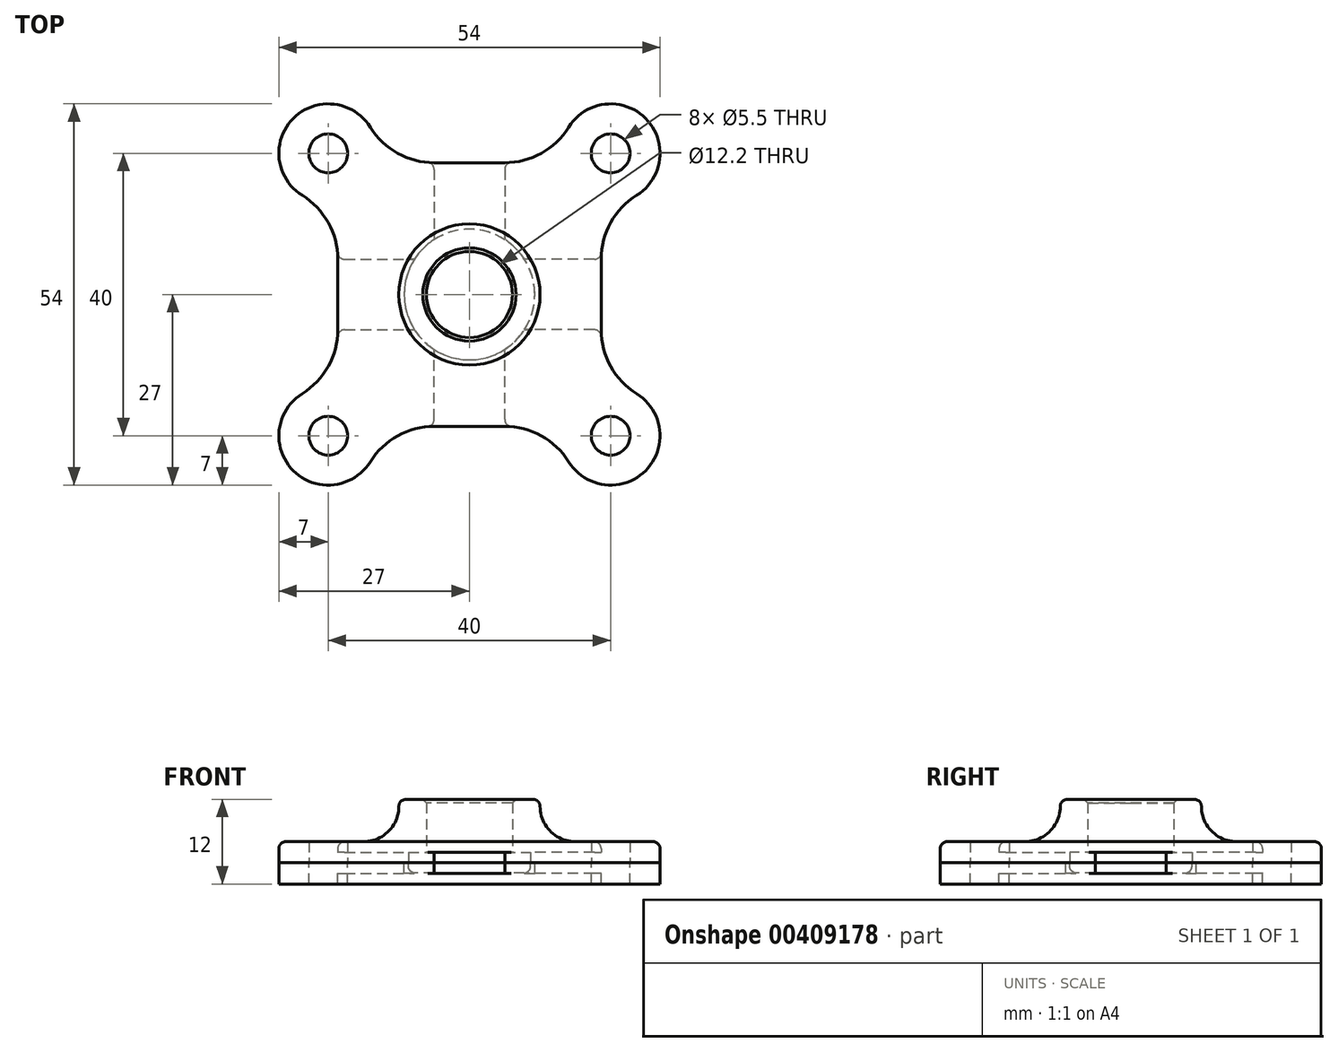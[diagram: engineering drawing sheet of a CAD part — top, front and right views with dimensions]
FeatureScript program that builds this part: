
annotation { "Feature Type Name" : "Feature", "Feature Type Description" : "" }
export const myFeature = defineFeature(function(context is Context, id is Id, definition is map)
    precondition{}
    {
        {
            var Q0;
            Q0=qCreatedBy(makeId("Top.planeOp"),FACE);
            var sketch = newSketch(context, id + "F0", { "sketchPlane" : qUnion([Q0])});
            skCircle(sketch, "E0", {"center": v(0, 0) * mm, "radius": 10 * mm});
            skCircle(sketch, "E1", {"center": v(0, 0) * mm, "radius": 6.1 * mm});
            skCircle(sketch, "E2", {"center": v(0, 0) * mm, "radius": 5 * mm});
            skCircle(sketch, "E3", {"center": v(0, 0) * mm, "radius": 9.25 * mm});
            skCircle(sketch, "E4", {"center": v(-20, 20) * mm, "radius": 2.75 * mm});
            skArc(sketch, "E5", {"start": v(-24.95, 24.95) * mm, "mid": v(-26.95, 19.2) * mm, "end": v(-23.7, 14.05) * mm});
            skLineSegment(sketch, "E6", {"start": v(-18.66, 5) * mm, "end": v(-8.66, 5) * mm});
            skArc(sketch, "E7", {"start": v(-23.7, 14.05) * mm, "mid": v(-20, 10.18) * mm, "end": v(-18.66, 5) * mm});
            skLineSegment(sketch, "E8", {"start": v(-20, 20) * mm, "end": v(0, 0) * mm, "construction": true});
            skLineSegment(sketch, "E9", {"start": v(-18.66, 5) * mm, "end": v(-18.66, 0) * mm});
            skArc(sketch, "E10.MirrorCS", {"start": v(-24.95, 24.95) * mm, "mid": v(-19.2, 26.95) * mm, "end": v(-14.05, 23.7) * mm});
            skArc(sketch, "E11.MirrorCS", {"start": v(-14.05, 23.7) * mm, "mid": v(-10.18, 20) * mm, "end": v(-5, 18.66) * mm});
            skLineSegment(sketch, "E12.MirrorCS", {"start": v(-5, 18.66) * mm, "end": v(-5, 8.66) * mm});
            skLineSegment(sketch, "E13.MirrorCS", {"start": v(-5, 18.66) * mm, "end": v(0, 18.66) * mm});
            skArc(sketch, "E14.1.0", {"start": v(-23.7, -14.05) * mm, "mid": v(-20, -10.18) * mm, "end": v(-18.66, -5) * mm});
            skLineSegment(sketch, "E14.1.1", {"start": v(-5, -18.66) * mm, "end": v(-5, -8.66) * mm});
            skArc(sketch, "E14.1.2", {"start": v(-24.95, -24.95) * mm, "mid": v(-26.95, -19.2) * mm, "end": v(-23.7, -14.05) * mm});
            skArc(sketch, "E14.1.3", {"start": v(-24.95, -24.95) * mm, "mid": v(-19.2, -26.95) * mm, "end": v(-14.05, -23.7) * mm});
            skLineSegment(sketch, "E14.1.4", {"start": v(-5, -18.66) * mm, "end": v(0, -18.66) * mm});
            skCircle(sketch, "E14.1.5", {"center": v(-20, -20) * mm, "radius": 2.75 * mm});
            skLineSegment(sketch, "E14.1.7", {"start": v(-18.66, -5) * mm, "end": v(-18.66, 0) * mm});
            skLineSegment(sketch, "E14.1.8", {"start": v(-18.66, -5) * mm, "end": v(-8.66, -5) * mm});
            skArc(sketch, "E14.1.9", {"start": v(-14.05, -23.7) * mm, "mid": v(-10.18, -20) * mm, "end": v(-5, -18.66) * mm});
            skLineSegment(sketch, "E14.1.10", {"start": v(-20, -20) * mm, "end": v(0, 0) * mm, "construction": true});
            skArc(sketch, "E14.2.0", {"start": v(14.05, -23.7) * mm, "mid": v(10.18, -20) * mm, "end": v(5, -18.66) * mm});
            skLineSegment(sketch, "E14.2.1", {"start": v(18.66, -5) * mm, "end": v(8.66, -5) * mm});
            skArc(sketch, "E14.2.2", {"start": v(24.95, -24.95) * mm, "mid": v(19.2, -26.95) * mm, "end": v(14.05, -23.7) * mm});
            skArc(sketch, "E14.2.3", {"start": v(24.95, -24.95) * mm, "mid": v(26.95, -19.2) * mm, "end": v(23.7, -14.05) * mm});
            skLineSegment(sketch, "E14.2.4", {"start": v(18.66, -5) * mm, "end": v(18.66, 0) * mm});
            skCircle(sketch, "E14.2.5", {"center": v(20, -20) * mm, "radius": 2.75 * mm});
            skLineSegment(sketch, "E14.2.7", {"start": v(5, -18.66) * mm, "end": v(0, -18.66) * mm});
            skLineSegment(sketch, "E14.2.8", {"start": v(5, -18.66) * mm, "end": v(5, -8.66) * mm});
            skArc(sketch, "E14.2.9", {"start": v(23.7, -14.05) * mm, "mid": v(20, -10.18) * mm, "end": v(18.66, -5) * mm});
            skLineSegment(sketch, "E14.2.10", {"start": v(20, -20) * mm, "end": v(0, 0) * mm, "construction": true});
            skArc(sketch, "E14.3.0", {"start": v(23.7, 14.05) * mm, "mid": v(20, 10.18) * mm, "end": v(18.66, 5) * mm});
            skLineSegment(sketch, "E14.3.1", {"start": v(5, 18.66) * mm, "end": v(5, 8.66) * mm});
            skArc(sketch, "E14.3.2", {"start": v(24.95, 24.95) * mm, "mid": v(26.95, 19.2) * mm, "end": v(23.7, 14.05) * mm});
            skArc(sketch, "E14.3.3", {"start": v(24.95, 24.95) * mm, "mid": v(19.2, 26.95) * mm, "end": v(14.05, 23.7) * mm});
            skLineSegment(sketch, "E14.3.4", {"start": v(5, 18.66) * mm, "end": v(0, 18.66) * mm});
            skCircle(sketch, "E14.3.5", {"center": v(20, 20) * mm, "radius": 2.75 * mm});
            skLineSegment(sketch, "E14.3.7", {"start": v(18.66, 5) * mm, "end": v(18.66, 0) * mm});
            skLineSegment(sketch, "E14.3.8", {"start": v(18.66, 5) * mm, "end": v(8.66, 5) * mm});
            skArc(sketch, "E14.3.9", {"start": v(14.05, 23.7) * mm, "mid": v(10.18, 20) * mm, "end": v(5, 18.66) * mm});
            skLineSegment(sketch, "E14.3.10", {"start": v(20, 20) * mm, "end": v(0, 0) * mm, "construction": true});
            skSolve(sketch);
        }
        {
            var Q0;
            {var subQ0=sQuery(id+"F0.wireOp",EDGE,"E14.2.1");Q0=makeQuery(id+"F0.imprint","IMPRINT",FACE,{"disambiguationData":[TD([[makeQuery(id+"F0.imprint","IMPRINT",EDGE,{"derivedFrom":subQ0}),-1.0]])]});}
            var Q1;
            Q1=makeQuery(id+"F0.imprint","IMPRINT",FACE,{"disambiguationData":[TD([[makeQuery(id+"F0.imprint","IMPRINT",EDGE,{"derivedFrom":sQuery(id+"F0.wireOp",EDGE,"E14.3.0")}),-1.0]])]});
            var Q2;
            Q2=makeQuery(id+"F0.imprint","IMPRINT",FACE,{"disambiguationData":[TD([[makeQuery(id+"F0.imprint","IMPRINT",EDGE,{"derivedFrom":sQuery(id+"F0.wireOp",EDGE,"E14.2.0")}),-1.0]])]});
            var Q3;
            Q3=makeQuery(id+"F0.imprint","IMPRINT",FACE,{"disambiguationData":[TD([[makeQuery(id+"F0.imprint","IMPRINT",EDGE,{"derivedFrom":sQuery(id+"F0.wireOp",EDGE,"E4")}),-1.0]])]});
            var Q4;
            Q4=makeQuery(id+"F0.imprint","IMPRINT",FACE,{"disambiguationData":[TD([[makeQuery(id+"F0.imprint","IMPRINT",EDGE,{"derivedFrom":sQuery(id+"F0.wireOp",EDGE,"E3")}),-1.0]])]});
            var Q5;
            Q5=makeQuery(id+"F0.imprint","IMPRINT",FACE,{"disambiguationData":[TD([[makeQuery(id+"F0.imprint","IMPRINT",EDGE,{"derivedFrom":sQuery(id+"F0.wireOp",EDGE,"E14.1.0")}),-1.0]])]});
            var Q6;
            {var subQ0=sQuery(id+"F0.wireOp",EDGE,"E14.1.1");Q6=makeQuery(id+"F0.imprint","IMPRINT",FACE,{"disambiguationData":[TD([[makeQuery(id+"F0.imprint","IMPRINT",EDGE,{"derivedFrom":subQ0}),-1.0]])]});}
            var Q7;
            Q7=makeQuery(id+"F0.imprint","IMPRINT",FACE,{"disambiguationData":[TD([[makeQuery(id+"F0.imprint","IMPRINT",EDGE,{"derivedFrom":sQuery(id+"F0.wireOp",EDGE,"E1")}),-1.0]])]});
            var Q8;
            {var subQ0=sQuery(id+"F0.wireOp",EDGE,"E6");Q8=makeQuery(id+"F0.imprint","IMPRINT",FACE,{"disambiguationData":[TD([[makeQuery(id+"F0.imprint","IMPRINT",EDGE,{"derivedFrom":subQ0}),-1.0]])]});}
            var Q9;
            {var subQ1=sQuery(id+"F0.wireOp",EDGE,"E12.MirrorCS");Q9=makeQuery(id+"F0.imprint","IMPRINT",FACE,{"disambiguationData":[TD([[makeQuery(id+"F0.imprint","IMPRINT",EDGE,{"derivedFrom":subQ1}),1.0]])]});}
            extrude(context, id + "F1", {"entities" : qUnion([Q0, Q1, Q2, Q3, Q4, Q5, Q6, Q7, Q8, Q9]), "depth" : 3 * mm, "offsetDistance" : 25 * mm});
        }
        {
            var Q0;
            Q0=makeQuery(id+"F0.imprint","IMPRINT",FACE,{"disambiguationData":[TD([[makeQuery(id+"F0.imprint","IMPRINT",EDGE,{"derivedFrom":sQuery(id+"F0.wireOp",EDGE,"E0")}),1.0]])]});
            var Q1;
            Q1=makeQuery(id+"F0.imprint","IMPRINT",FACE,{"disambiguationData":[TD([[makeQuery(id+"F0.imprint","IMPRINT",EDGE,{"derivedFrom":sQuery(id+"F0.wireOp",EDGE,"E1")}),-1.0]])]});
            extrude(context, id + "F2", {"entities" : qUnion([Q0, Q1]), "operationType" : NewBodyOperationType.ADD, "depth" : 9 * mm});
        }
        {
            var Q0;
            Q0=makeQuery(id+"F0.imprint","IMPRINT",FACE,{"disambiguationData":[TD([[makeQuery(id+"F0.imprint","IMPRINT",EDGE,{"derivedFrom":sQuery(id+"F0.wireOp",EDGE,"E1")}),-1.0]])]});
            var Q1;
            {var subQ0=sQuery(id+"F0.wireOp",EDGE,"5FznAjd5-Rlev-DzMA-E21E-VBbVsZXluKNu");Q1=makeQuery(id+"F0.imprint","IMPRINT",FACE,{"disambiguationData":[TD([[makeQuery(id+"F0.imprint","IMPRINT",EDGE,{"derivedFrom":subQ0}),1.0]])]});}
            var Q2;
            Q2=makeQuery(id+"F0.imprint","IMPRINT",FACE,{"disambiguationData":[TD([[makeQuery(id+"F0.imprint","IMPRINT",EDGE,{"derivedFrom":sQuery(id+"F0.wireOp",EDGE,"E3")}),-1.0]])]});
            var Q3;
            {var subQ1=sQuery(id+"F0.wireOp",EDGE,"bf5245d6-79ee-4a8b-a03c-ecbf48f2092a0.MirrorCS");Q3=makeQuery(id+"F0.imprint","IMPRINT",FACE,{"disambiguationData":[TD([[makeQuery(id+"F0.imprint","IMPRINT",EDGE,{"derivedFrom":subQ1}),-1.0]])]});}
            var Q4;
            {var subQ0=sQuery(id+"F0.wireOp",EDGE,"E14.1.1");Q4=makeQuery(id+"F0.imprint","IMPRINT",FACE,{"disambiguationData":[TD([[makeQuery(id+"F0.imprint","IMPRINT",EDGE,{"derivedFrom":subQ0}),-1.0]])]});}
            var Q5;
            {var subQ0=sQuery(id+"F0.wireOp",EDGE,"E6");Q5=makeQuery(id+"F0.imprint","IMPRINT",FACE,{"disambiguationData":[TD([[makeQuery(id+"F0.imprint","IMPRINT",EDGE,{"derivedFrom":subQ0}),-1.0]])]});}
            var Q6;
            {var subQ0=sQuery(id+"F0.wireOp",EDGE,"E14.2.1");Q6=makeQuery(id+"F0.imprint","IMPRINT",FACE,{"disambiguationData":[TD([[makeQuery(id+"F0.imprint","IMPRINT",EDGE,{"derivedFrom":subQ0}),-1.0]])]});}
            var Q7;
            {var subQ1=sQuery(id+"F0.wireOp",EDGE,"E12.MirrorCS");Q7=makeQuery(id+"F0.imprint","IMPRINT",FACE,{"disambiguationData":[TD([[makeQuery(id+"F0.imprint","IMPRINT",EDGE,{"derivedFrom":subQ1}),1.0]])]});}
            extrude(context, id + "F3", {"entities" : qUnion([Q0, Q1, Q2, Q3, Q4, Q5, Q6, Q7]), "operationType" : NewBodyOperationType.REMOVE, "depth" : 1.5 * mm, "offsetDistance" : 25 * mm});
        }
        {
            var Q0;
            Q0=makeQuery(id+"F0.imprint","IMPRINT",FACE,{"disambiguationData":[TD([[makeQuery(id+"F0.imprint","IMPRINT",EDGE,{"derivedFrom":sQuery(id+"F0.wireOp",EDGE,"E14.1.0")}),-1.0]])]});
            var Q1;
            {var subQ0=sQuery(id+"F0.wireOp",EDGE,"E14.1.1");Q1=makeQuery(id+"F0.imprint","IMPRINT",FACE,{"disambiguationData":[TD([[makeQuery(id+"F0.imprint","IMPRINT",EDGE,{"derivedFrom":subQ0}),-1.0]])]});}
            var Q2;
            Q2=makeQuery(id+"F0.imprint","IMPRINT",FACE,{"disambiguationData":[TD([[makeQuery(id+"F0.imprint","IMPRINT",EDGE,{"derivedFrom":sQuery(id+"F0.wireOp",EDGE,"E14.2.0")}),-1.0]])]});
            var Q3;
            {var subQ0=sQuery(id+"F0.wireOp",EDGE,"E14.2.1");Q3=makeQuery(id+"F0.imprint","IMPRINT",FACE,{"disambiguationData":[TD([[makeQuery(id+"F0.imprint","IMPRINT",EDGE,{"derivedFrom":subQ0}),-1.0]])]});}
            var Q4;
            Q4=makeQuery(id+"F0.imprint","IMPRINT",FACE,{"disambiguationData":[TD([[makeQuery(id+"F0.imprint","IMPRINT",EDGE,{"derivedFrom":sQuery(id+"F0.wireOp",EDGE,"E14.3.0")}),-1.0]])]});
            var Q5;
            {var subQ1=sQuery(id+"F0.wireOp",EDGE,"E12.MirrorCS");Q5=makeQuery(id+"F0.imprint","IMPRINT",FACE,{"disambiguationData":[TD([[makeQuery(id+"F0.imprint","IMPRINT",EDGE,{"derivedFrom":subQ1}),1.0]])]});}
            var Q6;
            Q6=makeQuery(id+"F0.imprint","IMPRINT",FACE,{"disambiguationData":[TD([[makeQuery(id+"F0.imprint","IMPRINT",EDGE,{"derivedFrom":sQuery(id+"F0.wireOp",EDGE,"E4")}),-1.0]])]});
            var Q7;
            {var subQ0=sQuery(id+"F0.wireOp",EDGE,"E6");Q7=makeQuery(id+"F0.imprint","IMPRINT",FACE,{"disambiguationData":[TD([[makeQuery(id+"F0.imprint","IMPRINT",EDGE,{"derivedFrom":subQ0}),-1.0]])]});}
            var Q8;
            Q8=makeQuery(id+"F0.imprint","IMPRINT",FACE,{"disambiguationData":[TD([[makeQuery(id+"F0.imprint","IMPRINT",EDGE,{"derivedFrom":sQuery(id+"F0.wireOp",EDGE,"E3")}),-1.0]])]});
            var Q9;
            Q9=makeQuery(id+"F0.imprint","IMPRINT",FACE,{"disambiguationData":[TD([[makeQuery(id+"F0.imprint","IMPRINT",EDGE,{"derivedFrom":sQuery(id+"F0.wireOp",EDGE,"E1")}),-1.0]])]});
            var Q10;
            Q10=makeQuery(id+"F0.imprint","IMPRINT",FACE,{"disambiguationData":[TD([[makeQuery(id+"F0.imprint","IMPRINT",EDGE,{"derivedFrom":sQuery(id+"F0.wireOp",EDGE,"E1")}),1.0]])]});
            var Q11;
            Q11=makeQuery(id+"F0.imprint","IMPRINT",FACE,{"disambiguationData":[TD([[makeQuery(id+"F0.imprint","IMPRINT",EDGE,{"derivedFrom":sQuery(id+"F0.wireOp",EDGE,"E2")}),1.0]])]});
            extrude(context, id + "F4", {"entities" : qUnion([Q0, Q1, Q2, Q3, Q4, Q5, Q6, Q7, Q8, Q9, Q10, Q11]), "oppositeDirection" : true, "depth" : 3 * mm, "offsetDistance" : 25 * mm});
        }
        {
            var Q0;
            {var subQ0=sQuery(id+"F0.wireOp",EDGE,"E6");Q0=makeQuery(id+"F0.imprint","IMPRINT",FACE,{"disambiguationData":[TD([[makeQuery(id+"F0.imprint","IMPRINT",EDGE,{"derivedFrom":subQ0}),-1.0]])]});}
            var Q1;
            Q1=makeQuery(id+"F0.imprint","IMPRINT",FACE,{"disambiguationData":[TD([[makeQuery(id+"F0.imprint","IMPRINT",EDGE,{"derivedFrom":sQuery(id+"F0.wireOp",EDGE,"E3")}),-1.0]])]});
            var Q2;
            {var subQ1=sQuery(id+"F0.wireOp",EDGE,"E12.MirrorCS");Q2=makeQuery(id+"F0.imprint","IMPRINT",FACE,{"disambiguationData":[TD([[makeQuery(id+"F0.imprint","IMPRINT",EDGE,{"derivedFrom":subQ1}),1.0]])]});}
            var Q3;
            {var subQ0=sQuery(id+"F0.wireOp",EDGE,"E14.2.1");Q3=makeQuery(id+"F0.imprint","IMPRINT",FACE,{"disambiguationData":[TD([[makeQuery(id+"F0.imprint","IMPRINT",EDGE,{"derivedFrom":subQ0}),-1.0]])]});}
            var Q4;
            {var subQ0=sQuery(id+"F0.wireOp",EDGE,"E14.1.1");Q4=makeQuery(id+"F0.imprint","IMPRINT",FACE,{"disambiguationData":[TD([[makeQuery(id+"F0.imprint","IMPRINT",EDGE,{"derivedFrom":subQ0}),-1.0]])]});}
            extrude(context, id + "F5", {"entities" : qUnion([Q0, Q1, Q2, Q3, Q4]), "operationType" : NewBodyOperationType.REMOVE, "oppositeDirection" : true, "depth" : 1.5 * mm, "offsetDistance" : 25 * mm});
        }
        {
            var Q0;
            Q0=makeQuery(id+"F2.opExtrude","CAP_EDGE",EDGE,{"disambiguationData":[OSD([sQuery(id+"F0.wireOp",EDGE,"E1")])],"isStart":false});
            var Q1;
            Q1=makeQuery(id+"F1.opExtrude","CAP_EDGE",EDGE,{"disambiguationData":[OSD([sQuery(id+"F0.wireOp",EDGE,"CR5xfrm7-slQB-9y9x-49ej-DvTKbvRHMWAN")])],"isStart":false});
            var Q2;
            Q2=makeQuery(id+"F1.opExtrude","CAP_EDGE",EDGE,{"disambiguationData":[OSD([sQuery(id+"F0.wireOp",EDGE,"M7DjQCVk-RdmV-3Hag-MnrL-rbCDdXIXaqB2")])],"isStart":false});
            var Q3;
            Q3=makeQuery(id+"F1.opExtrude","CAP_EDGE",EDGE,{"disambiguationData":[OSD([sQuery(id+"F0.wireOp",EDGE,"1c0b76fe-b687-46b7-8a7e-c5c0399cf78e0.MirrorC")])],"isStart":false});
            var Q4;
            Q4=makeQuery(id+"F1.opExtrude","CAP_EDGE",EDGE,{"disambiguationData":[OSD([sQuery(id+"F0.wireOp",EDGE,"bdfab768-ba76-4727-b505-0cc44eabfd0a0.MirrorC")])],"isStart":false});
            var Q5;
            Q5=makeQuery(id+"F1.opExtrude","CAP_EDGE",EDGE,{"disambiguationData":[OSD([sQuery(id+"F0.wireOp",EDGE,"bfb17f77-1127-425d-aafc-ff64732babe76.MirrorC")])],"isStart":false});
            chamfer(context, id + "F6", {"entities" : qUnion([Q0, Q1, Q2, Q3, Q4, Q5]), "width" : 0.5 * mm, "tangentPropagation" : true});
        }
        {
            var Q0;
            Q0=makeQuery(id+"F2.boolean.opBoolean","INTERSECT",EDGE,{"derivedFrom":[makeQuery(id+"F1.opExtrude","CAP_FACE",FACE,{"disambiguationData":[OSD([sQuery(id+"F0.wireOp",EDGE,"E1"),sQuery(id+"F0.wireOp",EDGE,"E4"),sQuery(id+"F0.wireOp",EDGE,"E5"),sQuery(id+"F0.wireOp",EDGE,"E7"),sQuery(id+"F0.wireOp",EDGE,"E9"),sQuery(id+"F0.wireOp",EDGE,"E10.MirrorCS"),sQuery(id+"F0.wireOp",EDGE,"E11.MirrorCS"),sQuery(id+"F0.wireOp",EDGE,"E13.MirrorCS"),sQuery(id+"F0.wireOp",EDGE,"E14.1.0"),sQuery(id+"F0.wireOp",EDGE,"E14.1.2"),sQuery(id+"F0.wireOp",EDGE,"E14.1.3"),sQuery(id+"F0.wireOp",EDGE,"E14.1.4"),sQuery(id+"F0.wireOp",EDGE,"E14.1.5"),sQuery(id+"F0.wireOp",EDGE,"E14.1.7"),sQuery(id+"F0.wireOp",EDGE,"E14.1.9"),sQuery(id+"F0.wireOp",EDGE,"E14.2.0"),sQuery(id+"F0.wireOp",EDGE,"E14.2.2"),sQuery(id+"F0.wireOp",EDGE,"E14.2.3"),sQuery(id+"F0.wireOp",EDGE,"E14.2.4"),sQuery(id+"F0.wireOp",EDGE,"E14.2.5"),sQuery(id+"F0.wireOp",EDGE,"E14.2.7"),sQuery(id+"F0.wireOp",EDGE,"E14.2.9"),sQuery(id+"F0.wireOp",EDGE,"E14.3.0"),sQuery(id+"F0.wireOp",EDGE,"E14.3.2"),sQuery(id+"F0.wireOp",EDGE,"E14.3.3"),sQuery(id+"F0.wireOp",EDGE,"E14.3.4"),sQuery(id+"F0.wireOp",EDGE,"E14.3.5"),sQuery(id+"F0.wireOp",EDGE,"E14.3.7"),sQuery(id+"F0.wireOp",EDGE,"E14.3.9")])],"isStart":false}),makeQuery(id+"F2.opExtrude","SWEPT_FACE",FACE,{"disambiguationData":[OSD([sQuery(id+"F0.wireOp",EDGE,"E0")])]})]});
            fillet(context, id + "F7", {"entities" : qUnion([Q0]), "radius" : 5 * mm, "tangentPropagation" : true, "allowEdgeOverflow" : false});
        }
        {
            var Q0;
            {var subQ0=sQuery(id+"F0.wireOp",EDGE,"E0");Q0=makeQuery(id+"F5.boolean.opBoolean","COPY",EDGE,{"derivedFrom":makeQuery(id+"F5.opExtrude","CAP_EDGE",EDGE,{"disambiguationData":[OSD([subQ0]),TDD([makeQuery(id+"F0.imprint","IMPRINT",EDGE,{"disambiguationData":[TD([[makeQuery(id+"F0.imprint","INTERSECT",VERTEX,{"derivedFrom":[subQ0,sQuery(id+"F0.wireOp",EDGE,"E6")]}),1.0]])],"derivedFrom":subQ0})])],"isStart":false})});}
            var Q1;
            {var subQ0=sQuery(id+"F0.wireOp",EDGE,"E0");Q1=makeQuery(id+"F5.boolean.opBoolean","COPY",EDGE,{"derivedFrom":makeQuery(id+"F5.opExtrude","CAP_EDGE",EDGE,{"disambiguationData":[OSD([subQ0]),TDD([makeQuery(id+"F0.imprint","IMPRINT",EDGE,{"disambiguationData":[TD([[makeQuery(id+"F0.imprint","INTERSECT",VERTEX,{"derivedFrom":[subQ0,sQuery(id+"F0.wireOp",EDGE,"E14.1.1")]}),1.0]])],"derivedFrom":subQ0})])],"isStart":false})});}
            var Q2;
            {var subQ0=sQuery(id+"F0.wireOp",EDGE,"E0");Q2=makeQuery(id+"F5.boolean.opBoolean","COPY",EDGE,{"derivedFrom":makeQuery(id+"F5.opExtrude","CAP_EDGE",EDGE,{"disambiguationData":[OSD([subQ0]),TDD([makeQuery(id+"F0.imprint","IMPRINT",EDGE,{"disambiguationData":[TD([[makeQuery(id+"F0.imprint","INTERSECT",VERTEX,{"derivedFrom":[subQ0,sQuery(id+"F0.wireOp",EDGE,"E14.2.1")]}),1.0]])],"derivedFrom":subQ0})])],"isStart":false})});}
            var Q3;
            {var subQ0=sQuery(id+"F0.wireOp",EDGE,"E0");Q3=makeQuery(id+"F5.boolean.opBoolean","COPY",EDGE,{"derivedFrom":makeQuery(id+"F5.opExtrude","CAP_EDGE",EDGE,{"disambiguationData":[OSD([subQ0]),TDD([makeQuery(id+"F0.imprint","IMPRINT",EDGE,{"disambiguationData":[TD([[makeQuery(id+"F0.imprint","INTERSECT",VERTEX,{"derivedFrom":[subQ0,sQuery(id+"F0.wireOp",EDGE,"E14.3.1")]}),1.0]])],"derivedFrom":subQ0})])],"isStart":false})});}
            var Q4;
            {var subQ0=sQuery(id+"F0.wireOp",EDGE,"E14.2.9");var subQ1=sQuery(id+"F0.wireOp",EDGE,"E14.2.4");var subQ2=sQuery(id+"F0.wireOp",EDGE,"E14.2.1");Q4=makeQuery(id+"F3.boolean.opBoolean","MERGE",EDGE,{"derivedFrom":[makeQuery(id+"F1.opExtrude","SWEPT_EDGE",EDGE,{"disambiguationData":[OSD([subQ2,subQ1,subQ0])]}),makeQuery(id+"F3.opExtrude","SWEPT_EDGE",EDGE,{"disambiguationData":[OSD([subQ2,subQ1,subQ0])]})]});}
            var Q5;
            {var subQ0=sQuery(id+"F0.wireOp",EDGE,"E14.2.9");var subQ1=sQuery(id+"F0.wireOp",EDGE,"E14.2.4");var subQ2=sQuery(id+"F0.wireOp",EDGE,"E14.2.1");Q5=makeQuery(id+"F5.boolean.opBoolean","MERGE",EDGE,{"derivedFrom":[makeQuery(id+"F4.opExtrude","SWEPT_EDGE",EDGE,{"disambiguationData":[OSD([subQ2,subQ1,subQ0])]}),makeQuery(id+"F5.opExtrude","SWEPT_EDGE",EDGE,{"disambiguationData":[OSD([subQ2,subQ1,subQ0])]})]});}
            var Q6;
            {var subQ0=sQuery(id+"F0.wireOp",EDGE,"E14.3.8");var subQ1=sQuery(id+"F0.wireOp",EDGE,"E14.3.7");var subQ2=sQuery(id+"F0.wireOp",EDGE,"E14.3.0");Q6=makeQuery(id+"F5.boolean.opBoolean","MERGE",EDGE,{"derivedFrom":[makeQuery(id+"F4.opExtrude","SWEPT_EDGE",EDGE,{"disambiguationData":[OSD([subQ2,subQ1,subQ0])]}),makeQuery(id+"F5.opExtrude","SWEPT_EDGE",EDGE,{"disambiguationData":[OSD([subQ2,subQ1,subQ0])]})]});}
            var Q7;
            {var subQ0=sQuery(id+"F0.wireOp",EDGE,"E14.3.8");var subQ1=sQuery(id+"F0.wireOp",EDGE,"E14.3.7");var subQ2=sQuery(id+"F0.wireOp",EDGE,"E14.3.0");Q7=makeQuery(id+"F3.boolean.opBoolean","MERGE",EDGE,{"derivedFrom":[makeQuery(id+"F1.opExtrude","SWEPT_EDGE",EDGE,{"disambiguationData":[OSD([subQ2,subQ1,subQ0])]}),makeQuery(id+"F3.opExtrude","SWEPT_EDGE",EDGE,{"disambiguationData":[OSD([subQ2,subQ1,subQ0])]})]});}
            var Q8;
            {var subQ0=sQuery(id+"F0.wireOp",EDGE,"E14.3.9");var subQ1=sQuery(id+"F0.wireOp",EDGE,"E14.3.4");var subQ2=sQuery(id+"F0.wireOp",EDGE,"E14.3.1");Q8=makeQuery(id+"F3.boolean.opBoolean","MERGE",EDGE,{"derivedFrom":[makeQuery(id+"F1.opExtrude","SWEPT_EDGE",EDGE,{"disambiguationData":[OSD([subQ2,subQ1,subQ0])]}),makeQuery(id+"F3.opExtrude","SWEPT_EDGE",EDGE,{"disambiguationData":[OSD([subQ2,subQ1,subQ0])]})]});}
            var Q9;
            {var subQ0=sQuery(id+"F0.wireOp",EDGE,"E14.3.9");var subQ1=sQuery(id+"F0.wireOp",EDGE,"E14.3.4");var subQ2=sQuery(id+"F0.wireOp",EDGE,"E14.3.1");Q9=makeQuery(id+"F5.boolean.opBoolean","MERGE",EDGE,{"derivedFrom":[makeQuery(id+"F4.opExtrude","SWEPT_EDGE",EDGE,{"disambiguationData":[OSD([subQ2,subQ1,subQ0])]}),makeQuery(id+"F5.opExtrude","SWEPT_EDGE",EDGE,{"disambiguationData":[OSD([subQ2,subQ1,subQ0])]})]});}
            var Q10;
            {var subQ0=sQuery(id+"F0.wireOp",EDGE,"E13.MirrorCS");var subQ1=sQuery(id+"F0.wireOp",EDGE,"E12.MirrorCS");var subQ2=sQuery(id+"F0.wireOp",EDGE,"E11.MirrorCS");Q10=makeQuery(id+"F3.boolean.opBoolean","MERGE",EDGE,{"derivedFrom":[makeQuery(id+"F1.opExtrude","SWEPT_EDGE",EDGE,{"disambiguationData":[OSD([subQ2,subQ1,subQ0])]}),makeQuery(id+"F3.opExtrude","SWEPT_EDGE",EDGE,{"disambiguationData":[OSD([subQ2,subQ1,subQ0])]})]});}
            var Q11;
            {var subQ0=sQuery(id+"F0.wireOp",EDGE,"E13.MirrorCS");var subQ1=sQuery(id+"F0.wireOp",EDGE,"E12.MirrorCS");var subQ2=sQuery(id+"F0.wireOp",EDGE,"E11.MirrorCS");Q11=makeQuery(id+"F5.boolean.opBoolean","MERGE",EDGE,{"derivedFrom":[makeQuery(id+"F4.opExtrude","SWEPT_EDGE",EDGE,{"disambiguationData":[OSD([subQ2,subQ1,subQ0])]}),makeQuery(id+"F5.opExtrude","SWEPT_EDGE",EDGE,{"disambiguationData":[OSD([subQ2,subQ1,subQ0])]})]});}
            var Q12;
            {var subQ0=sQuery(id+"F0.wireOp",EDGE,"E9");var subQ1=sQuery(id+"F0.wireOp",EDGE,"E7");var subQ2=sQuery(id+"F0.wireOp",EDGE,"E6");Q12=makeQuery(id+"F3.boolean.opBoolean","MERGE",EDGE,{"derivedFrom":[makeQuery(id+"F1.opExtrude","SWEPT_EDGE",EDGE,{"disambiguationData":[OSD([subQ2,subQ1,subQ0])]}),makeQuery(id+"F3.opExtrude","SWEPT_EDGE",EDGE,{"disambiguationData":[OSD([subQ2,subQ1,subQ0])]})]});}
            var Q13;
            {var subQ0=sQuery(id+"F0.wireOp",EDGE,"E9");var subQ1=sQuery(id+"F0.wireOp",EDGE,"E7");var subQ2=sQuery(id+"F0.wireOp",EDGE,"E6");Q13=makeQuery(id+"F5.boolean.opBoolean","MERGE",EDGE,{"derivedFrom":[makeQuery(id+"F4.opExtrude","SWEPT_EDGE",EDGE,{"disambiguationData":[OSD([subQ2,subQ1,subQ0])]}),makeQuery(id+"F5.opExtrude","SWEPT_EDGE",EDGE,{"disambiguationData":[OSD([subQ2,subQ1,subQ0])]})]});}
            var Q14;
            {var subQ0=sQuery(id+"F0.wireOp",EDGE,"E14.1.8");var subQ1=sQuery(id+"F0.wireOp",EDGE,"E14.1.7");var subQ2=sQuery(id+"F0.wireOp",EDGE,"E14.1.0");Q14=makeQuery(id+"F3.boolean.opBoolean","MERGE",EDGE,{"derivedFrom":[makeQuery(id+"F1.opExtrude","SWEPT_EDGE",EDGE,{"disambiguationData":[OSD([subQ2,subQ1,subQ0])]}),makeQuery(id+"F3.opExtrude","SWEPT_EDGE",EDGE,{"disambiguationData":[OSD([subQ2,subQ1,subQ0])]})]});}
            var Q15;
            {var subQ0=sQuery(id+"F0.wireOp",EDGE,"E14.1.8");var subQ1=sQuery(id+"F0.wireOp",EDGE,"E14.1.7");var subQ2=sQuery(id+"F0.wireOp",EDGE,"E14.1.0");Q15=makeQuery(id+"F5.boolean.opBoolean","MERGE",EDGE,{"derivedFrom":[makeQuery(id+"F4.opExtrude","SWEPT_EDGE",EDGE,{"disambiguationData":[OSD([subQ2,subQ1,subQ0])]}),makeQuery(id+"F5.opExtrude","SWEPT_EDGE",EDGE,{"disambiguationData":[OSD([subQ2,subQ1,subQ0])]})]});}
            var Q16;
            {var subQ0=sQuery(id+"F0.wireOp",EDGE,"E14.1.9");var subQ1=sQuery(id+"F0.wireOp",EDGE,"E14.1.4");var subQ2=sQuery(id+"F0.wireOp",EDGE,"E14.1.1");Q16=makeQuery(id+"F3.boolean.opBoolean","MERGE",EDGE,{"derivedFrom":[makeQuery(id+"F1.opExtrude","SWEPT_EDGE",EDGE,{"disambiguationData":[OSD([subQ2,subQ1,subQ0])]}),makeQuery(id+"F3.opExtrude","SWEPT_EDGE",EDGE,{"disambiguationData":[OSD([subQ2,subQ1,subQ0])]})]});}
            var Q17;
            {var subQ0=sQuery(id+"F0.wireOp",EDGE,"E14.1.9");var subQ1=sQuery(id+"F0.wireOp",EDGE,"E14.1.4");var subQ2=sQuery(id+"F0.wireOp",EDGE,"E14.1.1");Q17=makeQuery(id+"F5.boolean.opBoolean","MERGE",EDGE,{"derivedFrom":[makeQuery(id+"F4.opExtrude","SWEPT_EDGE",EDGE,{"disambiguationData":[OSD([subQ2,subQ1,subQ0])]}),makeQuery(id+"F5.opExtrude","SWEPT_EDGE",EDGE,{"disambiguationData":[OSD([subQ2,subQ1,subQ0])]})]});}
            var Q18;
            {var subQ0=sQuery(id+"F0.wireOp",EDGE,"E14.2.8");var subQ1=sQuery(id+"F0.wireOp",EDGE,"E14.2.7");var subQ2=sQuery(id+"F0.wireOp",EDGE,"E14.2.0");Q18=makeQuery(id+"F3.boolean.opBoolean","MERGE",EDGE,{"derivedFrom":[makeQuery(id+"F1.opExtrude","SWEPT_EDGE",EDGE,{"disambiguationData":[OSD([subQ2,subQ1,subQ0])]}),makeQuery(id+"F3.opExtrude","SWEPT_EDGE",EDGE,{"disambiguationData":[OSD([subQ2,subQ1,subQ0])]})]});}
            var Q19;
            {var subQ0=sQuery(id+"F0.wireOp",EDGE,"E14.2.8");var subQ1=sQuery(id+"F0.wireOp",EDGE,"E14.2.7");var subQ2=sQuery(id+"F0.wireOp",EDGE,"E14.2.0");Q19=makeQuery(id+"F5.boolean.opBoolean","MERGE",EDGE,{"derivedFrom":[makeQuery(id+"F4.opExtrude","SWEPT_EDGE",EDGE,{"disambiguationData":[OSD([subQ2,subQ1,subQ0])]}),makeQuery(id+"F5.opExtrude","SWEPT_EDGE",EDGE,{"disambiguationData":[OSD([subQ2,subQ1,subQ0])]})]});}
            var Q20;
            {var subQ0=sQuery(id+"F0.wireOp",EDGE,"E1");var subQ1=sQuery(id+"F0.wireOp",EDGE,"E0");Q20=makeQuery(id+"F7.opFillet","BLEND_EDGE",EDGE,{"blendedFrom":[makeQuery(id+"F2.boolean.opBoolean","INTERSECT",EDGE,{"derivedFrom":[makeQuery(id+"F1.opExtrude","CAP_FACE",FACE,{"disambiguationData":[OSD([subQ0,sQuery(id+"F0.wireOp",EDGE,"E4"),sQuery(id+"F0.wireOp",EDGE,"E5"),sQuery(id+"F0.wireOp",EDGE,"E7"),sQuery(id+"F0.wireOp",EDGE,"E9"),sQuery(id+"F0.wireOp",EDGE,"E10.MirrorCS"),sQuery(id+"F0.wireOp",EDGE,"E11.MirrorCS"),sQuery(id+"F0.wireOp",EDGE,"E13.MirrorCS"),sQuery(id+"F0.wireOp",EDGE,"E14.1.0"),sQuery(id+"F0.wireOp",EDGE,"E14.1.2"),sQuery(id+"F0.wireOp",EDGE,"E14.1.3"),sQuery(id+"F0.wireOp",EDGE,"E14.1.4"),sQuery(id+"F0.wireOp",EDGE,"E14.1.5"),sQuery(id+"F0.wireOp",EDGE,"E14.1.7"),sQuery(id+"F0.wireOp",EDGE,"E14.1.9"),sQuery(id+"F0.wireOp",EDGE,"E14.2.0"),sQuery(id+"F0.wireOp",EDGE,"E14.2.2"),sQuery(id+"F0.wireOp",EDGE,"E14.2.3"),sQuery(id+"F0.wireOp",EDGE,"E14.2.4"),sQuery(id+"F0.wireOp",EDGE,"E14.2.5"),sQuery(id+"F0.wireOp",EDGE,"E14.2.7"),sQuery(id+"F0.wireOp",EDGE,"E14.2.9"),sQuery(id+"F0.wireOp",EDGE,"E14.3.0"),sQuery(id+"F0.wireOp",EDGE,"E14.3.2"),sQuery(id+"F0.wireOp",EDGE,"E14.3.3"),sQuery(id+"F0.wireOp",EDGE,"E14.3.4"),sQuery(id+"F0.wireOp",EDGE,"E14.3.5"),sQuery(id+"F0.wireOp",EDGE,"E14.3.7"),sQuery(id+"F0.wireOp",EDGE,"E14.3.9")])],"isStart":false}),makeQuery(id+"F2.opExtrude","SWEPT_FACE",FACE,{"disambiguationData":[OSD([subQ1])]})]}),makeQuery(id+"F2.opExtrude","CAP_FACE",FACE,{"disambiguationData":[OSD([subQ1,subQ0])],"isStart":false})],"blendedInto":[makeQuery(id+"F2.opExtrude","CAP_FACE",FACE,{"disambiguationData":[OSD([subQ1,subQ0])],"isStart":false})]});}
            var Q21;
            Q21=makeQuery(id+"F1.opExtrude","CAP_EDGE",EDGE,{"disambiguationData":[OSD([sQuery(id+"F0.wireOp",EDGE,"E14.3.2"),sQuery(id+"F0.wireOp",EDGE,"E14.3.3")])],"isStart":false});
            var Q22;
            Q22=makeQuery(id+"F1.opExtrude","CAP_EDGE",EDGE,{"disambiguationData":[OSD([sQuery(id+"F0.wireOp",EDGE,"E5"),sQuery(id+"F0.wireOp",EDGE,"E10.MirrorCS")])],"isStart":false});
            var Q23;
            Q23=makeQuery(id+"F1.opExtrude","CAP_EDGE",EDGE,{"disambiguationData":[OSD([sQuery(id+"F0.wireOp",EDGE,"E14.1.2"),sQuery(id+"F0.wireOp",EDGE,"E14.1.3")])],"isStart":false});
            var Q24;
            Q24=makeQuery(id+"F1.opExtrude","CAP_EDGE",EDGE,{"disambiguationData":[OSD([sQuery(id+"F0.wireOp",EDGE,"E14.2.2"),sQuery(id+"F0.wireOp",EDGE,"E14.2.3")])],"isStart":false});
            var Q25;
            Q25=makeQuery(id+"F1.opExtrude","CAP_EDGE",EDGE,{"disambiguationData":[OSD([sQuery(id+"F0.wireOp",EDGE,"E14.2.4"),sQuery(id+"F0.wireOp",EDGE,"E14.3.7")])],"isStart":false});
            var Q26;
            Q26=makeQuery(id+"F1.opExtrude","CAP_EDGE",EDGE,{"disambiguationData":[OSD([sQuery(id+"F0.wireOp",EDGE,"E13.MirrorCS"),sQuery(id+"F0.wireOp",EDGE,"E14.3.4")])],"isStart":false});
            var Q27;
            Q27=makeQuery(id+"F1.opExtrude","CAP_EDGE",EDGE,{"disambiguationData":[OSD([sQuery(id+"F0.wireOp",EDGE,"E9"),sQuery(id+"F0.wireOp",EDGE,"E14.1.7")])],"isStart":false});
            var Q28;
            Q28=makeQuery(id+"F1.opExtrude","CAP_EDGE",EDGE,{"disambiguationData":[OSD([sQuery(id+"F0.wireOp",EDGE,"E14.1.4"),sQuery(id+"F0.wireOp",EDGE,"E14.2.7")])],"isStart":false});
            var Q29;
            Q29=makeQuery(id+"F2.opExtrude","CAP_EDGE",EDGE,{"disambiguationData":[OSD([sQuery(id+"F0.wireOp",EDGE,"E0")])],"isStart":false});
            fillet(context, id + "F8", {"entities" : qUnion([Q0, Q1, Q2, Q3, Q4, Q5, Q6, Q7, Q8, Q9, Q10, Q11, Q12, Q13, Q14, Q15, Q16, Q17, Q18, Q19, Q20, Q21, Q22, Q23, Q24, Q25, Q26, Q27, Q28, Q29]), "radius" : 1 * mm, "tangentPropagation" : true, "allowEdgeOverflow" : false});
        }
    });
